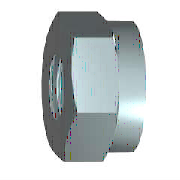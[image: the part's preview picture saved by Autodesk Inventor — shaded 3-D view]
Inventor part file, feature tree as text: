
AUTODESK INVENTOR PART (.ipt)
format: ipt  version: 2019 (Build 230136000, 136)  size: 187,904 bytes
history: native  units: mm (DEFAULTED — no unit token found)
features: sketch x4, extrude x1, chamfer x1, hole x1, other x1, plane x1
ambient origin geometry x7: Origin, YZ Plane, XZ Plane, X Axis, Y Axis, Z Axis, Center Point
bodies: Solid1 (feature_tree), Body (feature_tree)
feature tree (9):
  extrude  "Ring"  Depth=4.4mm
  chamfer  "Chamfer1"  Distance=8.0mm
  hole  "Thread"  [1 undecoded]
  other  "Work Axis1"
  plane  "Work Plane1"
  sketch  "Sketch1"  dims[d0=9.237604mm d1=4.4mm]
  sketch  "Sketch3"  dims[d3=30.0deg]
  sketch  "Sketch2"  dims[d2=0.0mm]
  sketch  "Sketch4"  dims[d4=30.0deg d5=8.0mm d6=8.0mm d26=90.0deg d7=8.0mm d8=2.4mm d9=0.0mm d30=4.134mm d31=6.0mm d32=4.0mm d33=2.0mm d34=14.3117mm d35=8.0mm d36=20.594885mm d10=0.433013mm d11=30.0deg d12=0.433013mm d13=30.0deg d14=0.0mm d15=0.0mm d45=0.0mm d46=0.433013mm d47=0.433013mm d48=0.0mm]
note: 1 required parameter value undecoded (feature->parameter linkage not recoverable at this tier; creation-order binding heuristic only, values carry confidence <= 0.55)
